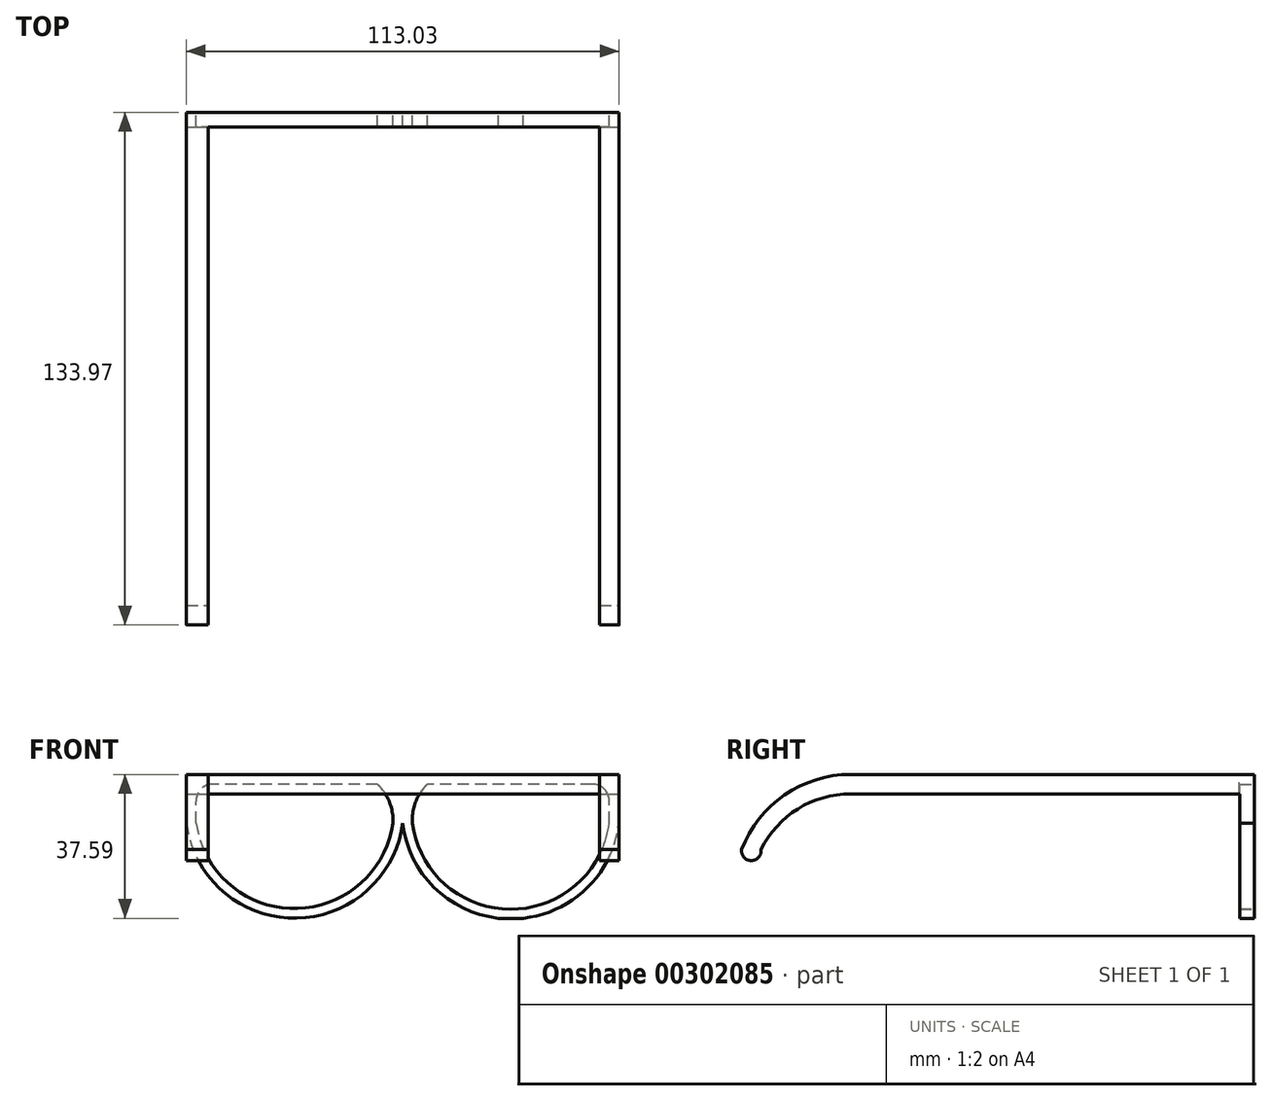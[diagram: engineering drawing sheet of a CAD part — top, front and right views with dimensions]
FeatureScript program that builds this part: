
annotation { "Feature Type Name" : "Feature", "Feature Type Description" : "" }
export const myFeature = defineFeature(function(context is Context, id is Id, definition is map)
    precondition{}
    {
        {
            var Q0;
            Q0=qCreatedBy(makeId("Front.planeOp"),FACE);
            var sketch = newSketch(context, id + "F0", { "sketchPlane" : qUnion([Q0])});
            skLineSegment(sketch, "E0", {"start": v(-64.27, 19.64) * mm, "end": v(48.76, 19.64) * mm});
            skLineSegment(sketch, "E1", {"start": v(17.21, -17.95) * mm, "end": v(23.78, -17.95) * mm});
            skLineSegment(sketch, "E2", {"start": v(-64.27, 19.64) * mm, "end": v(-64.27, 6.94) * mm});
            skLineSegment(sketch, "E3", {"start": v(48.76, 19.64) * mm, "end": v(48.76, 6.94) * mm});
            skArc(sketch, "E4", {"start": v(-7.76, 6.94) * mm, "mid": v(20.5, -18.14) * mm, "end": v(48.76, 6.94) * mm});
            skLineSegment(sketch, "E5.bottom", {"start": v(-64.27, 19.64) * mm, "end": v(-61.73, 19.64) * mm});
            skLineSegment(sketch, "E5.left", {"start": v(-64.27, 19.64) * mm, "end": v(-64.27, 17.1) * mm});
            skLineSegment(sketch, "E6.bottom", {"start": v(48.76, 19.64) * mm, "end": v(46.22, 19.64) * mm});
            skLineSegment(sketch, "E6.left", {"start": v(48.76, 19.64) * mm, "end": v(48.76, 17.1) * mm});
            skLineSegment(sketch, "E7", {"start": v(41.77, 17.1) * mm, "end": v(-1.34, 17.1) * mm});
            skLineSegment(sketch, "E8", {"start": v(-61.73, 6.93) * mm, "end": v(-61.73, 12.66) * mm});
            skLineSegment(sketch, "E9", {"start": v(-7.76, 6.94) * mm, "end": v(-5.22, 6.94) * mm});
            skLineSegment(sketch, "E10", {"start": v(-7.76, 6.94) * mm, "end": v(-10.3, 6.94) * mm});
            skArc(sketch, "E11", {"start": v(-64.27, 6.94) * mm, "mid": v(-36.02, -17.95) * mm, "end": v(-7.76, 6.94) * mm});
            skLineSegment(sketch, "E12", {"start": v(-36.02, -17.95) * mm, "end": v(-36.02, -17.95) * mm});
            skLineSegment(sketch, "E13", {"start": v(20.5, -18.14) * mm, "end": v(20.5, -17.95) * mm});
            skArc(sketch, "E14", {"start": v(-61.73, 6.93) * mm, "mid": v(-36.01, -15.4) * mm, "end": v(-10.3, 6.94) * mm});
            skArc(sketch, "E15", {"start": v(-5.22, 6.94) * mm, "mid": v(20.5, -15.6) * mm, "end": v(46.22, 6.94) * mm});
            skArc(sketch, "E16", {"start": v(-1.34, 17.1) * mm, "mid": v(-4.36, 12.44) * mm, "end": v(-5.22, 6.94) * mm});
            skArc(sketch, "E17", {"start": v(-10.3, 6.94) * mm, "mid": v(-11.22, 12.45) * mm, "end": v(-14.31, 17.1) * mm});
            skLineSegment(sketch, "E18", {"start": v(46.22, 6.94) * mm, "end": v(46.22, 12.66) * mm});
            skArc(sketch, "E19", {"start": v(-57.29, 17.1) * mm, "mid": v(-60.43, 15.8) * mm, "end": v(-61.73, 12.66) * mm});
            skArc(sketch, "E20", {"start": v(46.22, 12.66) * mm, "mid": v(44.91, 15.8) * mm, "end": v(41.77, 17.1) * mm});
            skPoint(sketch, "E21.orphan", {"position": v(46.22, 17.1) * mm});
            skPoint(sketch, "E22.orphan", {"position": v(-7.76, -17.95) * mm});
            skPoint(sketch, "E23.end.orphan", {"position": v(-64.27, -17.95) * mm});
            skPoint(sketch, "E24.orphan", {"position": v(48.76, -17.95) * mm});
            skPoint(sketch, "E25.orphan", {"position": v(-61.73, 17.1) * mm});
            skPoint(sketch, "E26.end.orphan", {"position": v(-7.76, 17.1) * mm});
            skPoint(sketch, "E27.orphan", {"position": v(-7.76, 19.64) * mm});
            skLineSegment(sketch, "E28.trimOffspring", {"start": v(-14.31, 17.1) * mm, "end": v(-57.29, 17.1) * mm});
            skSolve(sketch);
        }
        {
            var Q0;
            Q0=makeQuery(id+"F0.imprint","IMPRINT",FACE,{"disambiguationData":[TD([[makeQuery(id+"F0.imprint","IMPRINT",EDGE,{"derivedFrom":sQuery(id+"F0.wireOp",EDGE,"E0")}),-1.0]])]});
            extrude(context, id + "F1", {"entities" : qUnion([Q0]), "depth" : 3.8 * mm});
        }
        {
            var Q0;
            Q0=makeQuery(id+"F1.opExtrude","SWEPT_FACE",FACE,{"disambiguationData":[OSD([sQuery(id+"F0.wireOp",EDGE,"E3"),sQuery(id+"F0.wireOp",EDGE,"E6.left")])]});
            var sketch = newSketch(context, id + "F2", { "sketchPlane" : qUnion([Q0])});
            skLineSegment(sketch, "E29.bottom", {"start": v(-3.81, 19.64) * mm, "end": v(-105.4, 19.64) * mm});
            skLineSegment(sketch, "E29.top", {"start": v(-3.81, 14.56) * mm, "end": v(-105.4, 14.56) * mm});
            skLineSegment(sketch, "E29.left", {"start": v(-3.81, 19.64) * mm, "end": v(-3.81, 14.56) * mm});
            skArc(sketch, "E30", {"start": v(-105.4, 14.56) * mm, "mid": v(-119.21, 10.63) * mm, "end": v(-128.86, 0) * mm});
            skArc(sketch, "E31", {"start": v(-105.4, 19.64) * mm, "mid": v(-122.73, 14.26) * mm, "end": v(-133.94, 0) * mm});
            skArc(sketch, "E32", {"start": v(-133.94, 0) * mm, "mid": v(-131.4, -2.9) * mm, "end": v(-128.86, 0) * mm});
            skSolve(sketch);
        }
        {
            var Q0;
            Q0=makeQuery(id+"F2.imprint","IMPRINT",FACE,{"disambiguationData":[TD([[makeQuery(id+"F2.imprint","IMPRINT",EDGE,{"derivedFrom":sQuery(id+"F2.wireOp",EDGE,"E29.bottom")}),1.0]])]});
            extrude(context, id + "F3", {"entities" : qUnion([Q0]), "operationType" : NewBodyOperationType.ADD, "oppositeDirection" : true, "depth" : 113.03 * mm});
        }
        {
            var Q0;
            Q0=makeQuery(id+"F3.boolean.opBoolean","MERGE",FACE,{"derivedFrom":[makeQuery(id+"F1.opExtrude","SWEPT_FACE",FACE,{"disambiguationData":[OSD([sQuery(id+"F0.wireOp",EDGE,"E0"),sQuery(id+"F0.wireOp",EDGE,"E5.bottom"),sQuery(id+"F0.wireOp",EDGE,"E6.bottom")])]}),makeQuery(id+"F3.opExtrude","SWEPT_FACE",FACE,{"disambiguationData":[OSD([sQuery(id+"F2.wireOp",EDGE,"E29.bottom")])]})]});
            var sketch = newSketch(context, id + "F4", { "sketchPlane" : qUnion([Q0])});
            skLineSegment(sketch, "E33.bottom", {"start": v(-64.27, 0) * mm, "end": v(-58.58, 0) * mm});
            skLineSegment(sketch, "E33.top", {"start": v(-64.27, -5.7) * mm, "end": v(-58.58, -5.7) * mm});
            skLineSegment(sketch, "E33.left", {"start": v(-64.27, 0) * mm, "end": v(-64.27, -5.7) * mm});
            skLineSegment(sketch, "E33.right", {"start": v(-58.58, 0) * mm, "end": v(-58.58, -5.7) * mm});
            skLineSegment(sketch, "E34.bottom", {"start": v(48.76, 0) * mm, "end": v(43.68, 0) * mm});
            skLineSegment(sketch, "E34.top", {"start": v(48.76, -5.08) * mm, "end": v(43.68, -5.08) * mm});
            skLineSegment(sketch, "E34.left", {"start": v(48.76, 0) * mm, "end": v(48.76, -5.08) * mm});
            skLineSegment(sketch, "E34.right", {"start": v(43.68, 0) * mm, "end": v(43.68, -5.08) * mm});
            skLineSegment(sketch, "E35.bottom", {"start": v(-58.58, -5.7) * mm, "end": v(43.68, -5.7) * mm});
            skLineSegment(sketch, "E35.top", {"start": v(-58.58, -169.37) * mm, "end": v(43.68, -169.37) * mm});
            skLineSegment(sketch, "E35.left", {"start": v(-58.58, -5.7) * mm, "end": v(-58.58, -169.37) * mm});
            skLineSegment(sketch, "E35.right", {"start": v(43.68, -5.7) * mm, "end": v(43.68, -169.37) * mm});
            skSolve(sketch);
        }
        {
            var Q0;
            {var subQ0=sQuery(id+"F4.wireOp",EDGE,"E35.top");Q0=makeQuery(id+"F4.imprint","IMPRINT",FACE,{"disambiguationData":[TD([[makeQuery(id+"F4.imprint","IMPRINT",EDGE,{"derivedFrom":subQ0}),1.0]])]});}
            var Q1;
            {var subQ0=sQuery(id+"F4.wireOp",EDGE,"E35.bottom");Q1=makeQuery(id+"F4.imprint","IMPRINT",FACE,{"disambiguationData":[TD([[makeQuery(id+"F4.imprint","IMPRINT",EDGE,{"derivedFrom":subQ0}),-1.0]])]});}
            extrude(context, id + "F5", {"entities" : qUnion([Q0, Q1]), "operationType" : NewBodyOperationType.REMOVE, "oppositeDirection" : true, "depth" : 76.2 * mm});
        }
        {
            var Q0;
            Q0=makeQuery(id+"F5.boolean.opBoolean","COPY",FACE,{"derivedFrom":makeQuery(id+"F5.opExtrude","SWEPT_FACE",FACE,{"disambiguationData":[OSD([sQuery(id+"F4.wireOp",EDGE,"E35.bottom")])]})});
            extrude(context, id + "F6", {"entities" : qUnion([Q0]), "operationType" : NewBodyOperationType.REMOVE, "oppositeDirection" : true, "depth" : 1.78 * mm});
        }
    });
